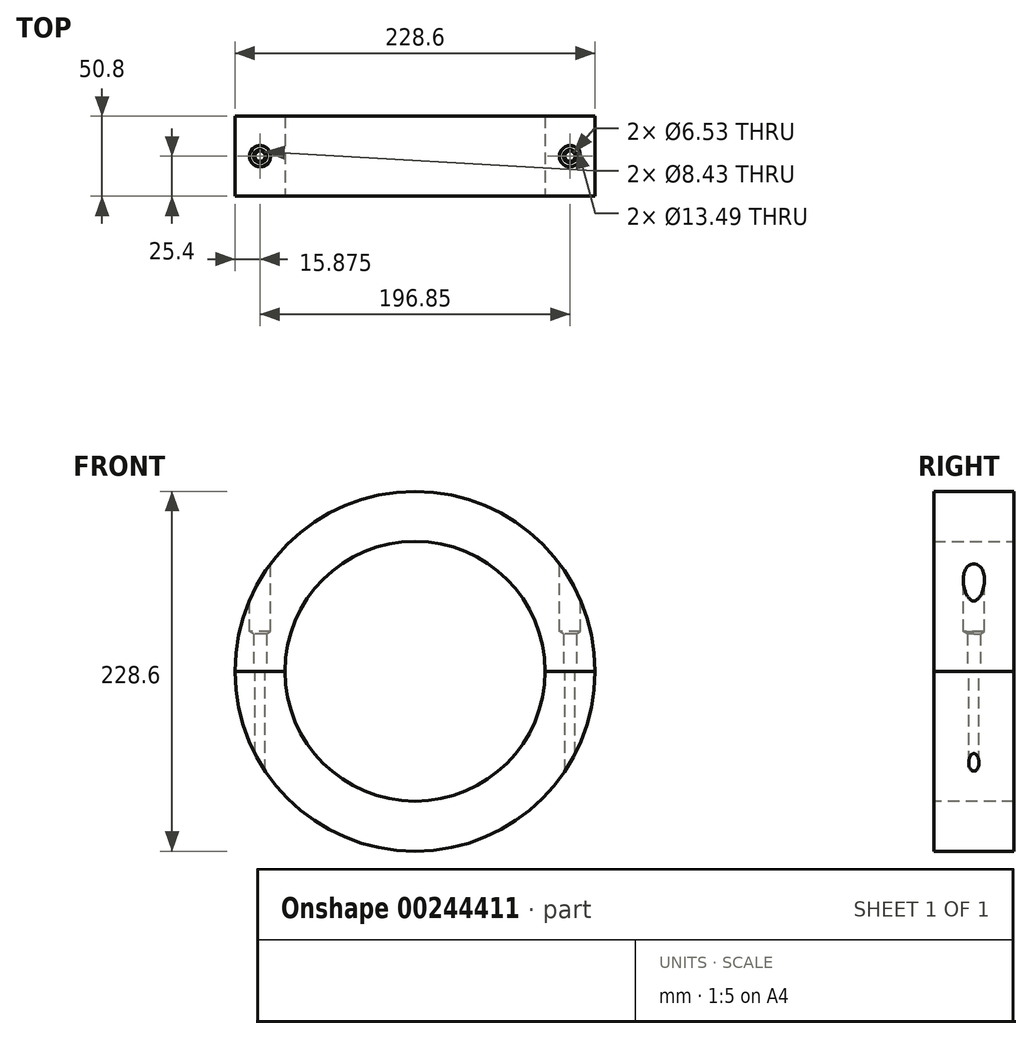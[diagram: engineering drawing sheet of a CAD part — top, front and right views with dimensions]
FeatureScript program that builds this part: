
annotation { "Feature Type Name" : "Feature", "Feature Type Description" : "" }
export const myFeature = defineFeature(function(context is Context, id is Id, definition is map)
    precondition{}
    {
        {
            var Q0;
            Q0=qCreatedBy(makeId("Front.planeOp"),FACE);
            var sketch = newSketch(context, id + "F0", { "sketchPlane" : qUnion([Q0])});
            skArc(sketch, "E0", {"start": v(114.3, 0) * mm, "mid": v(0, 114.3) * mm, "end": v(-114.3, 0) * mm});
            skArc(sketch, "E1", {"start": v(82.55, 0) * mm, "mid": v(0, 82.55) * mm, "end": v(-82.55, 0) * mm});
            skLineSegment(sketch, "E2", {"start": v(-114.3, 0) * mm, "end": v(-82.55, 0) * mm});
            skLineSegment(sketch, "E3.trimOffspring", {"start": v(82.55, 0) * mm, "end": v(114.3, 0) * mm});
            skSolve(sketch);
        }
        {
            var Q0;
            Q0 = qSketchRegion(id + "F0", true);
            extrude(context, id + "F1", {"entities" : qUnion([Q0]), "endBound" : BoundingType.SYMMETRIC, "depth" : 50.8 * mm});
        }
        {
            var Q0;
            Q0=makeQuery(id+"F1.opExtrude","CAP_FACE",FACE,{"disambiguationData":[OSD([sQuery(id+"F0.wireOp",EDGE,"E0"),sQuery(id+"F0.wireOp",EDGE,"E1"),sQuery(id+"F0.wireOp",EDGE,"E2"),sQuery(id+"F0.wireOp",EDGE,"E3.trimOffspring")])],"isStart":false});
            var sketch = newSketch(context, id + "F2", { "sketchPlane" : qUnion([Q0])});
            skArc(sketch, "E4", {"start": v(-82.55, 0) * mm, "mid": v(0, -82.55) * mm, "end": v(82.55, 0) * mm});
            skArc(sketch, "E5", {"start": v(-114.3, 0) * mm, "mid": v(0, -114.3) * mm, "end": v(114.3, 0) * mm});
            skLineSegment(sketch, "E6", {"start": v(-114.3, 0) * mm, "end": v(-82.55, 0) * mm});
            skLineSegment(sketch, "E7", {"start": v(82.55, 0) * mm, "end": v(114.3, 0) * mm});
            skSolve(sketch);
        }
        {
            var Q0;
            Q0 = qSketchRegion(id + "F2", true);
            var Q1;
            Q1=makeQuery(id+"F1.opExtrude","CAP_FACE",FACE,{"disambiguationData":[OSD([sQuery(id+"F0.wireOp",EDGE,"E0"),sQuery(id+"F0.wireOp",EDGE,"E1"),sQuery(id+"F0.wireOp",EDGE,"E2"),sQuery(id+"F0.wireOp",EDGE,"E3.trimOffspring")])],"isStart":true});
            extrude(context, id + "F3", {"entities" : qUnion([Q0]), "endBound" : BoundingType.UP_TO_SURFACE, "oppositeDirection" : true, "endBoundEntityFace" : qUnion([Q1]), "depth" : 25.4 * mm});
        }
        {
            var Q0;
            Q0=makeQuery(id+"F3.opExtrude","SWEPT_FACE",FACE,{"disambiguationData":[OSD([sQuery(id+"F2.wireOp",EDGE,"E6")])]});
            var sketch = newSketch(context, id + "F4", { "sketchPlane" : qUnion([Q0])});
            skLineSegment(sketch, "E8", {"start": v(-114.3, 25.4) * mm, "end": v(-82.55, -25.4) * mm, "construction": true});
            skLineSegment(sketch, "E9", {"start": v(114.3, 25.4) * mm, "end": v(82.55, -25.4) * mm, "construction": true});
            skPoint(sketch, "E10", {"position": v(-98.43, 0) * mm});
            skPoint(sketch, "E11", {"position": v(98.43, 0) * mm});
            skSolve(sketch);
        }
        {
            var Q0;
            Q0=sQuery(id+"F4.wireOp",VERTEX,"E10");
            var Q1;
            Q1=sQuery(id+"F4.wireOp",VERTEX,"E11");
            var Q2;
            Q2=makeQuery(id+"F3.opExtrude","SWEPT_BODY",BODY,{"disambiguationData":[OSD([sQuery(id+"F2.wireOp",EDGE,"E4"),sQuery(id+"F2.wireOp",EDGE,"E5"),sQuery(id+"F2.wireOp",EDGE,"E6"),sQuery(id+"F2.wireOp",EDGE,"E7")])]});
            hole(context, id + "F5", {"style" : HoleStyle.SIMPLE, "endStyle" : HoleEndStyle.THROUGH, "standardTappedOrClearance" : lookupTablePath({ "standard" : "ANSI", "engagement" : "75%", "pitch" : "18 tpi", "size" : "5/16", "type" : "Tapped" }), "standardBlindInLast" : lookupTablePath({ "standard" : "ANSI", "engagement" : "75%", "pitch" : "18 tpi", "size" : "5/16", "type" : "Tapped" }), "holeDiameter" : 6.53 * mm, "showTappedDepth" : true, "tappedDepth" : 12.7 * mm, "tapClearance" : 3, "startFromSketch" : true, "locations" : qUnion([Q0, Q1]), "scope" : qUnion([Q2]), "majorDiameter" : 7.94 * mm});
        }
        {
            var Q0;
            Q0=makeQuery(id+"F1.opExtrude","SWEPT_FACE",FACE,{"disambiguationData":[OSD([sQuery(id+"F0.wireOp",EDGE,"E2")])]});
            var sketch = newSketch(context, id + "F6", { "sketchPlane" : qUnion([Q0])});
            skPoint(sketch, "E12", {"position": v(-98.43, 0) * mm});
            skPoint(sketch, "E13", {"position": v(98.43, 0) * mm});
            skSolve(sketch);
        }
        {
            var Q0;
            Q0=sQuery(id+"F6.wireOp",VERTEX,"E12");
            var Q1;
            Q1=sQuery(id+"F6.wireOp",VERTEX,"E13");
            var Q2;
            Q2=makeQuery(id+"F1.opExtrude","SWEPT_BODY",BODY,{"disambiguationData":[OSD([sQuery(id+"F0.wireOp",EDGE,"E0"),sQuery(id+"F0.wireOp",EDGE,"E1"),sQuery(id+"F0.wireOp",EDGE,"E2"),sQuery(id+"F0.wireOp",EDGE,"E3.trimOffspring")])]});
            hole(context, id + "F7", {"style" : HoleStyle.SIMPLE, "endStyle" : HoleEndStyle.THROUGH, "standardTappedOrClearance" : lookupTablePath({ "standard" : "ANSI", "fit" : "Normal (ASME)", "size" : "5/16", "type" : "Clearance" }), "standardBlindInLast" : lookupTablePath({ "fit" : "Free", "standard" : "ANSI", "size" : "5/16", "type" : "Clearance" }), "holeDiameter" : 8.43 * mm, "tappedDepth" : 12.7 * mm, "tapClearance" : 3, "startFromSketch" : true, "locations" : qUnion([Q0, Q1]), "scope" : qUnion([Q2])});
        }
        {
            var Q0;
            Q0=qCreatedBy(makeId("Front.planeOp"),FACE);
            var sketch = newSketch(context, id + "F8", { "sketchPlane" : qUnion([Q0])});
            skLineSegment(sketch, "E14", {"start": v(0, 0) * mm, "end": v(0, 114.3) * mm});
            skSolve(sketch);
        }
        {
            var Q0;
            Q0=sQuery(id+"F8.wireOp",EDGE,"E14");
            var Q1;
            Q1=sQuery(id+"F8.wireOp",VERTEX,"E14.end");
            cPlane(context, id + "F9", {"entities" : qUnion([Q0, Q1]), "cplaneType" : CPlaneType.LINE_POINT, "offset" : 25.4 * mm, "width" : 152.4 * mm, "height" : 152.4 * mm});
        }
        {
            var Q0;
            Q0=qCreatedBy(id+"F9.planeOp",FACE);
            var sketch = newSketch(context, id + "F10", { "sketchPlane" : qUnion([Q0])});
            skPoint(sketch, "E15", {"position": v(-98.43, 0) * mm});
            skPoint(sketch, "E16", {"position": v(98.43, 0) * mm});
            skSolve(sketch);
        }
        {
            var Q0;
            Q0=sQuery(id+"F10.wireOp",VERTEX,"E15");
            var Q1;
            Q1=sQuery(id+"F10.wireOp",VERTEX,"E16");
            var Q2;
            Q2=makeQuery(id+"F1.opExtrude","SWEPT_BODY",BODY,{"disambiguationData":[OSD([sQuery(id+"F0.wireOp",EDGE,"E0"),sQuery(id+"F0.wireOp",EDGE,"E1"),sQuery(id+"F0.wireOp",EDGE,"E2"),sQuery(id+"F0.wireOp",EDGE,"E3.trimOffspring")])]});
            hole(context, id + "F11", {"style" : HoleStyle.SIMPLE, "endStyle" : HoleEndStyle.BLIND, "standardTappedOrClearance" : lookupTablePath({ "standard" : "ANSI", "fit" : "Normal (ASME)", "size" : "1/2", "type" : "Clearance" }), "standardBlindInLast" : lookupTablePath({ "fit" : "Free", "standard" : "ANSI", "size" : "1/2", "type" : "Clearance" }), "holeDiameter" : 13.5 * mm, "holeDepth" : 88.9 * mm, "tappedDepth" : 12.7 * mm, "tapClearance" : 3, "startFromSketch" : true, "locations" : qUnion([Q0, Q1]), "scope" : qUnion([Q2])});
        }
        {
            var Q0;
            Q0=makeQuery(id+"F1.opExtrude","CAP_FACE",FACE,{"disambiguationData":[OSD([sQuery(id+"F0.wireOp",EDGE,"E0"),sQuery(id+"F0.wireOp",EDGE,"E1"),sQuery(id+"F0.wireOp",EDGE,"E2"),sQuery(id+"F0.wireOp",EDGE,"E3.trimOffspring")])],"isStart":false});
            var sketch = newSketch(context, id + "F12", { "sketchPlane" : qUnion([Q0])});
            skLineSegment(sketch, "E17", {"start": v(0, 0) * mm, "end": v(-80.82, 80.82) * mm, "construction": true});
            skLineSegment(sketch, "E18", {"start": v(0, 0) * mm, "end": v(80.82, 80.82) * mm, "construction": true});
            skLineSegment(sketch, "E19", {"start": v(0, 0) * mm, "end": v(0, 41.35) * mm, "construction": true});
            skSolve(sketch);
        }
        {
            var Q0;
            Q0=sQuery(id+"F12.wireOp",EDGE,"E17");
            var Q1;
            Q1=sQuery(id+"F12.wireOp",VERTEX,"E17.end");
            cPlane(context, id + "F13", {"entities" : qUnion([Q0, Q1]), "cplaneType" : CPlaneType.LINE_POINT, "offset" : 25.4 * mm, "width" : 152.4 * mm, "height" : 152.4 * mm});
        }
        {
            var Q0;
            Q0=qCreatedBy(id+"F13.planeOp",FACE);
            var sketch = newSketch(context, id + "F14", { "sketchPlane" : qUnion([Q0])});
            skPoint(sketch, "E20", {"position": v(0, 0) * mm});
            skSolve(sketch);
        }
        {
            var Q0;
            Q0=sQuery(id+"F12.wireOp",EDGE,"E18");
            var Q1;
            Q1=sQuery(id+"F12.wireOp",VERTEX,"E18.end");
            cPlane(context, id + "F15", {"entities" : qUnion([Q0, Q1]), "cplaneType" : CPlaneType.LINE_POINT, "offset" : 25.4 * mm, "width" : 152.4 * mm, "height" : 152.4 * mm});
        }
    });
